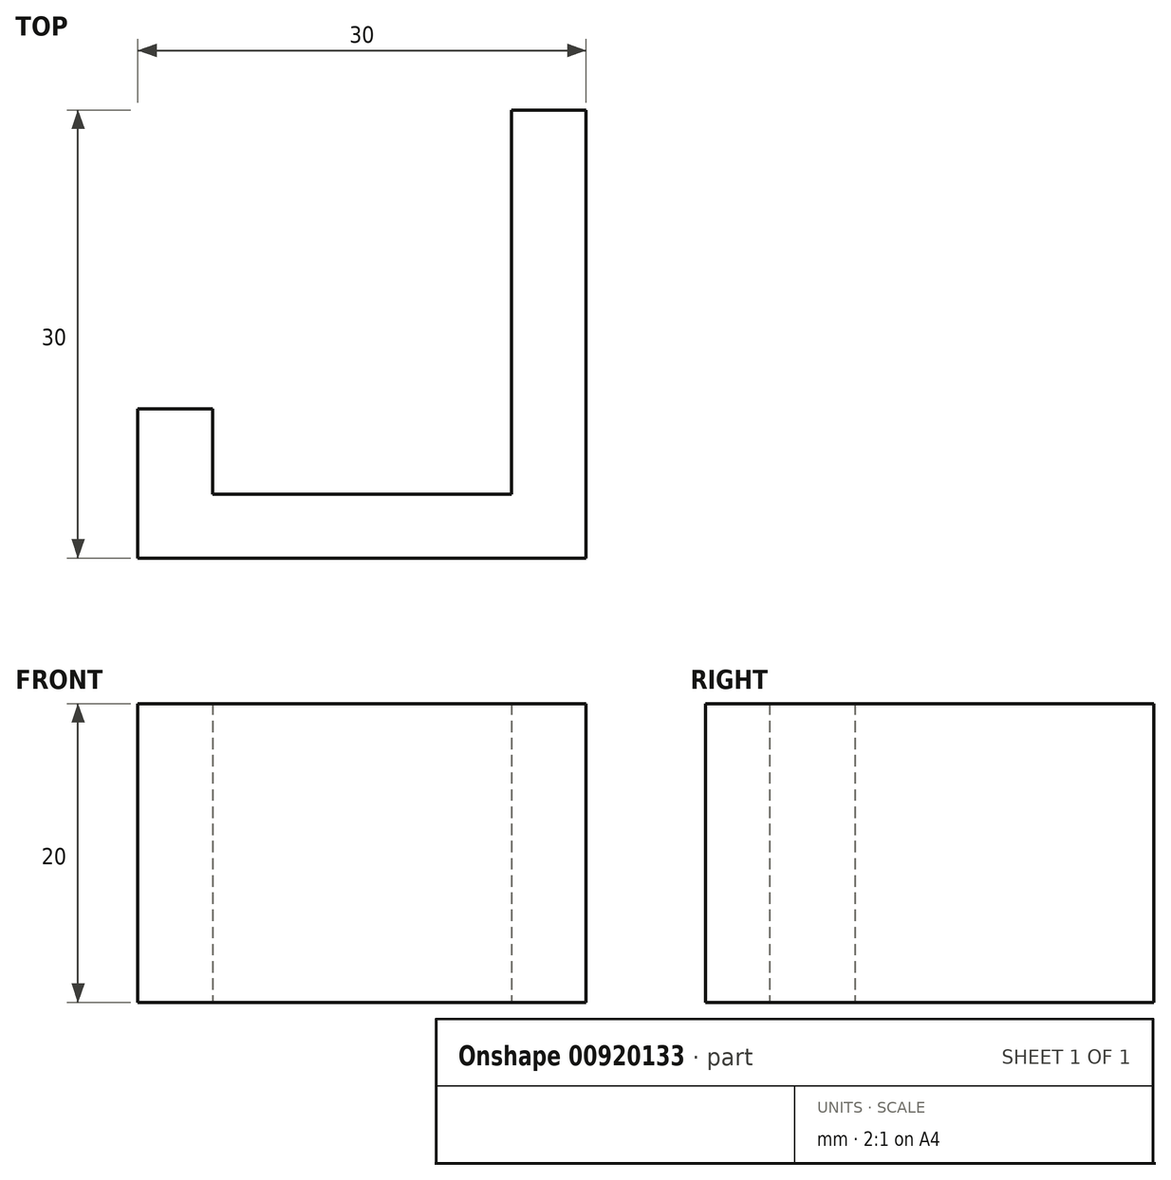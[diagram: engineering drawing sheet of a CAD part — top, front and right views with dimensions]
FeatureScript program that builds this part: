
annotation { "Feature Type Name" : "Feature", "Feature Type Description" : "" }
export const myFeature = defineFeature(function(context is Context, id is Id, definition is map)
    precondition{}
    {
        {
            var Q0;
            Q0=qCreatedBy(makeId("Top.planeOp"),FACE);
            var sketch = newSketch(context, id + "F0", { "sketchPlane" : qUnion([Q0])});
            skLineSegment(sketch, "E0.bottom", {"start": v(2.5, 15) * mm, "end": v(-2.5, 15) * mm});
            skLineSegment(sketch, "E0.top", {"start": v(2.5, -15) * mm, "end": v(-2.5, -15) * mm});
            skLineSegment(sketch, "E0.left", {"start": v(2.5, 15) * mm, "end": v(2.5, -15) * mm});
            skLineSegment(sketch, "E0.right", {"start": v(-2.5, 15) * mm, "end": v(-2.5, -10.71) * mm});
            skPoint(sketch, "E0.middle", {"position": v(0, 0) * mm});
            skLineSegment(sketch, "E1.bottom", {"start": v(2.5, -15) * mm, "end": v(-27.5, -15) * mm});
            skLineSegment(sketch, "E1.top", {"start": v(-2.5, -10.71) * mm, "end": v(-22.5, -10.71) * mm});
            skLineSegment(sketch, "E1.left", {"start": v(2.5, -15) * mm, "end": v(2.5, -10.71) * mm});
            skLineSegment(sketch, "E1.right", {"start": v(-27.5, -15) * mm, "end": v(-27.5, -10.71) * mm});
            skLineSegment(sketch, "E2.bottom", {"start": v(-27.5, -15) * mm, "end": v(-22.5, -15) * mm});
            skLineSegment(sketch, "E2.top", {"start": v(-27.5, -5) * mm, "end": v(-22.5, -5) * mm});
            skLineSegment(sketch, "E2.left", {"start": v(-27.5, -15) * mm, "end": v(-27.5, -5) * mm});
            skLineSegment(sketch, "E2.right", {"start": v(-22.5, -10.71) * mm, "end": v(-22.5, -5) * mm});
            skSolve(sketch);
        }
        {
            var Q0;
            Q0 = qSketchRegion(id + "F0", true);
            extrude(context, id + "F1", {"entities" : qUnion([Q0]), "depth" : 20 * mm, "offsetDistance" : 25 * mm});
        }
    });
